# Revit family: Safety & Protection_Barrier_UltiGroup_Column Protector
name_source: partatom
category: Generic Models
revit_build: Autodesk Revit Architecture 2016 (Build: 20150220_1215(x64)
units: mm (PartAtom-declared; Revit-internal decimal feet)

## family parameters
Always vertical = Yes
Can host rebar = No
Cut with Voids When Loaded = No
OmniClass Number = 23.30.80.17.17
OmniClass Title = Column Protectors
Part Type = Normal
Room Calculation Point = No
Round Connector Dimension = Use Diameter
Shared = No
Work Plane-Based = No

## types (3) — shared parameters
500-1500 span = No
Cover caps = Cover caps
Fax = 07 846 2467
GRS = GRS
Manufacturer = UltiGroup
Model = Ulti Impactable Column Protector - COPRO 90
PVC Black = PVC Black
PVC yellow = PVC Yellow
Send Message = http://ultigroup.co.nz
URL = www.ultigroup.co.nz
zero-valued in all types: InstallationGroup_ANZRS, ModifiedIssue_ANZRS

## per-type parameters (varying)
| type | Column Protector Size | Description |
| 500mm x 500mm | 500 mm  [stored 1.64042 ft] | Impactable PVC Column Protector 500 x 500 |
| 600mm x 600mm | 600 mm | Impactable PVC Column Protector 600 x 600 |
| 700mm x 700mm | 700 mm | Impactable PVC Column Protector 700 x 700 |

note: [stored X ft] marks values corroborated as IEEE doubles in the binary element streams (Revit-internal decimal feet)

## geometry (parser evidence)
native form markers: Sweep x2
no freeform markers — native parametric forms only
